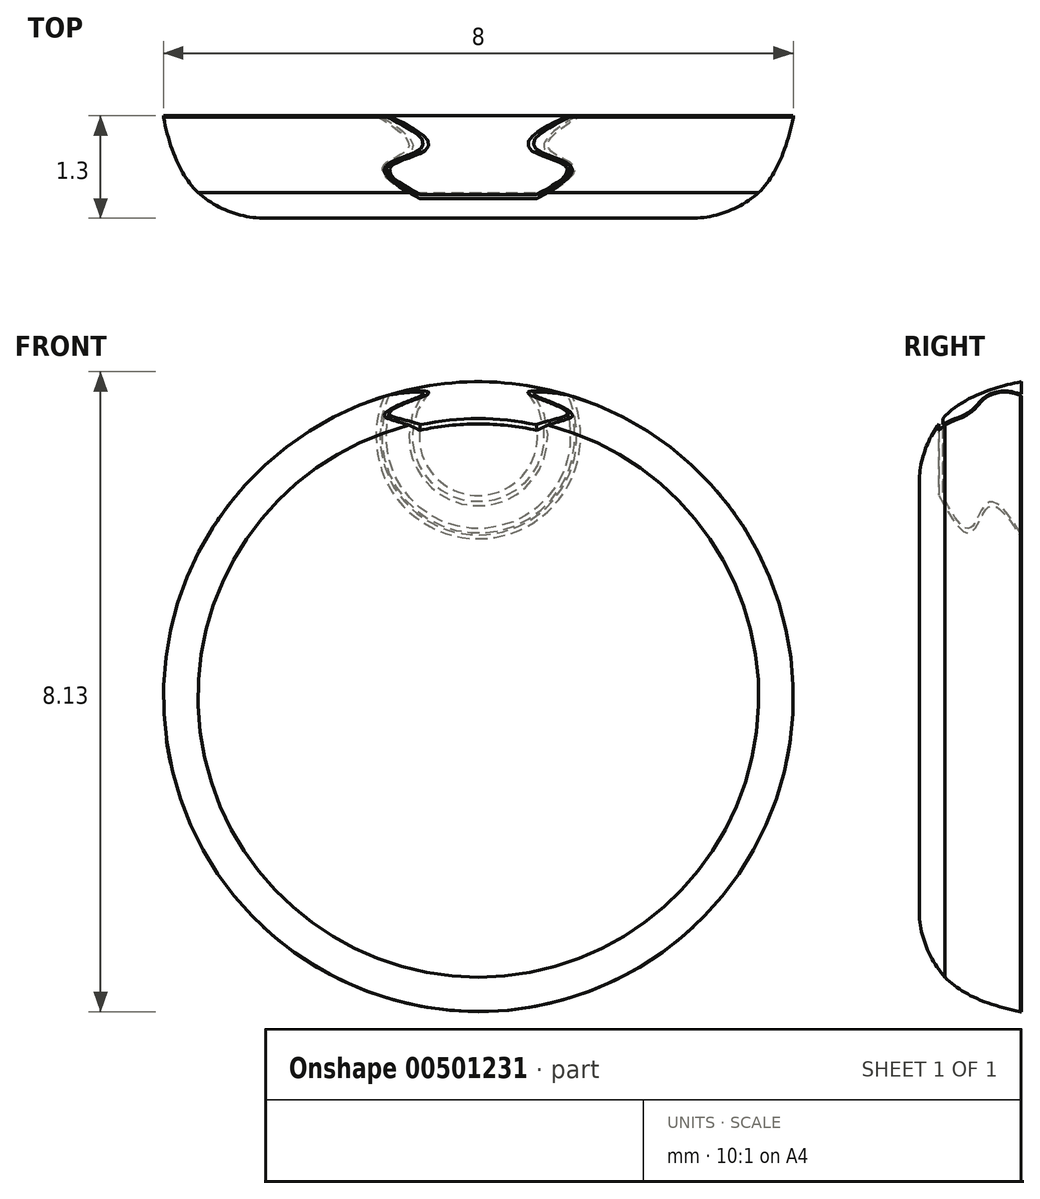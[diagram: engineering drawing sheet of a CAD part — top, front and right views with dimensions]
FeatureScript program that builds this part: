
annotation { "Feature Type Name" : "Feature", "Feature Type Description" : "" }
export const myFeature = defineFeature(function(context is Context, id is Id, definition is map)
    precondition{}
    {
        {
            var Q0;
            Q0=qCreatedBy(makeId("Front.planeOp"),FACE);
            var sketch = newSketch(context, id + "F0", { "sketchPlane" : qUnion([Q0])});
            skCircle(sketch, "E0", {"center": v(0, 0) * mm, "radius": 4 * mm});
            skCircle(sketch, "E1", {"center": v(0, 3.3) * mm, "radius": 1.25 * mm});
            skLineSegment(sketch, "E2", {"start": v(-1.25, 3.3) * mm, "end": v(1.25, 3.3) * mm, "construction": true});
            skLineSegment(sketch, "E3", {"start": v(0, 3.3) * mm, "end": v(-1.13, 3.84) * mm, "construction": true});
            skLineSegment(sketch, "E4.MirrorCS", {"start": v(0, 3.3) * mm, "end": v(1.13, 3.84) * mm, "construction": true});
            skPoint(sketch, "E5", {"position": v(0, 2.06) * mm});
            skPoint(sketch, "E6", {"position": v(0, 4) * mm});
            skSolve(sketch);
        }
        {
            var Q0;
            Q0=qCreatedBy(makeId("Right.planeOp"),FACE);
            var sketch = newSketch(context, id + "F1", { "sketchPlane" : qUnion([Q0])});
            skLineSegment(sketch, "E7", {"start": v(0, 4) * mm, "end": v(-1.3, 4) * mm});
            skLineSegment(sketch, "E8", {"start": v(-1.3, 4) * mm, "end": v(-1.3, 0) * mm});
            skLineSegment(sketch, "E9", {"start": v(-1.3, 0) * mm, "end": v(0, 0) * mm});
            skLineSegment(sketch, "E10", {"start": v(0, 0) * mm, "end": v(0, 4) * mm});
            skLineSegment(sketch, "E11", {"start": v(0, 3.3) * mm, "end": v(-1, 3.3) * mm});
            skLineSegment(sketch, "E12", {"start": v(-1, 3.3) * mm, "end": v(-1.05, 3.3) * mm});
            skLineSegment(sketch, "E13", {"start": v(-1.05, 3.3) * mm, "end": v(-1.05, 2.56) * mm});
            skPoint(sketch, "E14.0", {"position": v(0, 2.06) * mm});
            skLineSegment(sketch, "E15", {"start": v(-1, 3.3) * mm, "end": v(-1, 2.56) * mm});
            skFitSpline(sketch, "E16", {"points": [v(-1, 2.56) * mm, v(0, 2.06) * mm], "startDerivative": vector(1.78, -3.64) * mm, "endDerivative": vector(2.13, -3.62) * mm});
            skPoint(sketch, "E17", {"position": v(0, 2) * mm});
            skFitSpline(sketch, "E18", {"points": [v(-1.05, 2.56) * mm, v(0, 2) * mm], "startDerivative": vector(2.04, -4) * mm, "endDerivative": vector(2.1, -3.69) * mm});
            skLineSegment(sketch, "E19", {"start": v(-1.3, 4) * mm, "end": v(-1.3, 4.8) * mm});
            skLineSegment(sketch, "E20", {"start": v(-1.3, 4.8) * mm, "end": v(0, 4.8) * mm});
            skLineSegment(sketch, "E21", {"start": v(0, 4.8) * mm, "end": v(0, 4) * mm});
            skSolve(sketch);
        }
        {
            var Q0;
            {var subQ3=sQuery(id+"F1.wireOp",EDGE,"E7");Q0=makeQuery(id+"F1.imprint","IMPRINT",FACE,{"disambiguationData":[TD([[makeQuery(id+"F1.imprint","IMPRINT",EDGE,{"derivedFrom":subQ3}),1.0]])]});}
            var Q1;
            {var subQ0=sQuery(id+"F1.wireOp",EDGE,"E11");Q1=makeQuery(id+"F1.imprint","IMPRINT",FACE,{"disambiguationData":[TD([[makeQuery(id+"F1.imprint","IMPRINT",EDGE,{"derivedFrom":subQ0}),1.0]])]});}
            var Q2;
            Q2=makeQuery(id+"F1.imprint","IMPRINT",FACE,{"disambiguationData":[TD([[makeQuery(id+"F1.imprint","IMPRINT",EDGE,{"derivedFrom":sQuery(id+"F1.wireOp",EDGE,"E12")}),1.0]])]});
            var Q3;
            Q3=sQuery(id+"F1.wireOp",EDGE,"E9");
            revolve(context, id + "F2", {"entities" : qUnion([Q0, Q1, Q2]), "axis" : qUnion([Q3]), "revolveType" : RevolveType.FULL});
        }
        {
            var Q0;
            Q0=makeQuery(id+"F1.imprint","IMPRINT",FACE,{"disambiguationData":[TD([[makeQuery(id+"F1.imprint","IMPRINT",EDGE,{"derivedFrom":sQuery(id+"F1.wireOp",EDGE,"E12")}),1.0]])]});
            var Q1;
            {var subQ0=sQuery(id+"F1.wireOp",EDGE,"E11");Q1=makeQuery(id+"F1.imprint","IMPRINT",FACE,{"disambiguationData":[TD([[makeQuery(id+"F1.imprint","IMPRINT",EDGE,{"derivedFrom":subQ0}),1.0]])]});}
            var Q2;
            Q2=sQuery(id+"F1.wireOp",EDGE,"E11");
            revolve(context, id + "F3", {"operationType" : NewBodyOperationType.REMOVE, "entities" : qUnion([Q0, Q1]), "axis" : qUnion([Q2]), "revolveType" : RevolveType.FULL, "oppositeDirection" : true});
        }
        {
            var Q0;
            {var subQ0=sQuery(id+"F1.wireOp",EDGE,"E11");Q0=makeQuery(id+"F1.imprint","IMPRINT",FACE,{"disambiguationData":[TD([[makeQuery(id+"F1.imprint","IMPRINT",EDGE,{"derivedFrom":subQ0}),1.0]])]});}
            var Q1;
            Q1=sQuery(id+"F1.wireOp",EDGE,"E11");
            revolve(context, id + "F4", {"entities" : qUnion([Q0]), "axis" : qUnion([Q1]), "revolveType" : RevolveType.FULL});
        }
        {
            var Q0;
            Q0=makeQuery(id+"F2.opRevolve","SWEPT_EDGE",EDGE,{"disambiguationData":[OSD([sQuery(id+"F1.wireOp",EDGE,"E7"),sQuery(id+"F1.wireOp",EDGE,"E8")])]});
            fillet(context, id + "F5", {"entities" : qUnion([Q0]), "radius" : 1.3 * mm, "tangentPropagation" : true, "allowEdgeOverflow" : false});
        }
        {
            var Q0;
            Q0=makeQuery(id+"F1.imprint","IMPRINT",FACE,{"disambiguationData":[TD([[makeQuery(id+"F1.imprint","IMPRINT",EDGE,{"derivedFrom":sQuery(id+"F1.wireOp",EDGE,"E7")}),-1.0]])]});
            var Q1;
            Q1=sQuery(id+"F1.wireOp",EDGE,"E9");
            revolve(context, id + "F6", {"operationType" : NewBodyOperationType.REMOVE, "entities" : qUnion([Q0]), "axis" : qUnion([Q1]), "revolveType" : RevolveType.FULL, "oppositeDirection" : true});
        }
        {
            var Q0;
            Q0=makeQuery(id+"F6.boolean.opBoolean","INTERSECT",EDGE,{"derivedFrom":[makeQuery(id+"F4.opRevolve","SWEPT_FACE",FACE,{"disambiguationData":[OSD([sQuery(id+"F1.wireOp",EDGE,"E15")])]}),makeQuery(id+"F6.opRevolve","SWEPT_FACE",FACE,{"disambiguationData":[OSD([sQuery(id+"F1.wireOp",EDGE,"E7")])]})]});
            fillet(context, id + "F7", {"entities" : qUnion([Q0]), "radius" : .1 * mm, "tangentPropagation" : true, "allowEdgeOverflow" : false});
        }
        {
            var Q0;
            Q0=qCreatedBy(makeId("Right.planeOp"),FACE);
            var sketch = newSketch(context, id + "F8", { "sketchPlane" : qUnion([Q0])});
            skFitSpline(sketch, "E22", {"points": [v(-1.2, 3.21) * mm, v(0, 4) * mm], "startDerivative": vector(0.54, 1.21) * mm, "endDerivative": vector(2.1, 0.42) * mm});
            skLineSegment(sketch, "E23", {"start": v(0, 0) * mm, "end": v(-1.53, 0) * mm});
            skLineSegment(sketch, "E24", {"start": v(0, 4) * mm, "end": v(-1.2, 4) * mm});
            skLineSegment(sketch, "E25", {"start": v(-1.2, 4) * mm, "end": v(-1.2, 3.21) * mm});
            skSolve(sketch);
        }
        {
            var Q0;
            Q0 = qSketchRegion(id + "F8", true);
            var Q1;
            Q1=sQuery(id+"F8.wireOp",EDGE,"E23");
            revolve(context, id + "F9", {"operationType" : NewBodyOperationType.REMOVE, "entities" : qUnion([Q0]), "axis" : qUnion([Q1]), "revolveType" : RevolveType.FULL, "oppositeDirection" : true});
        }
    });
